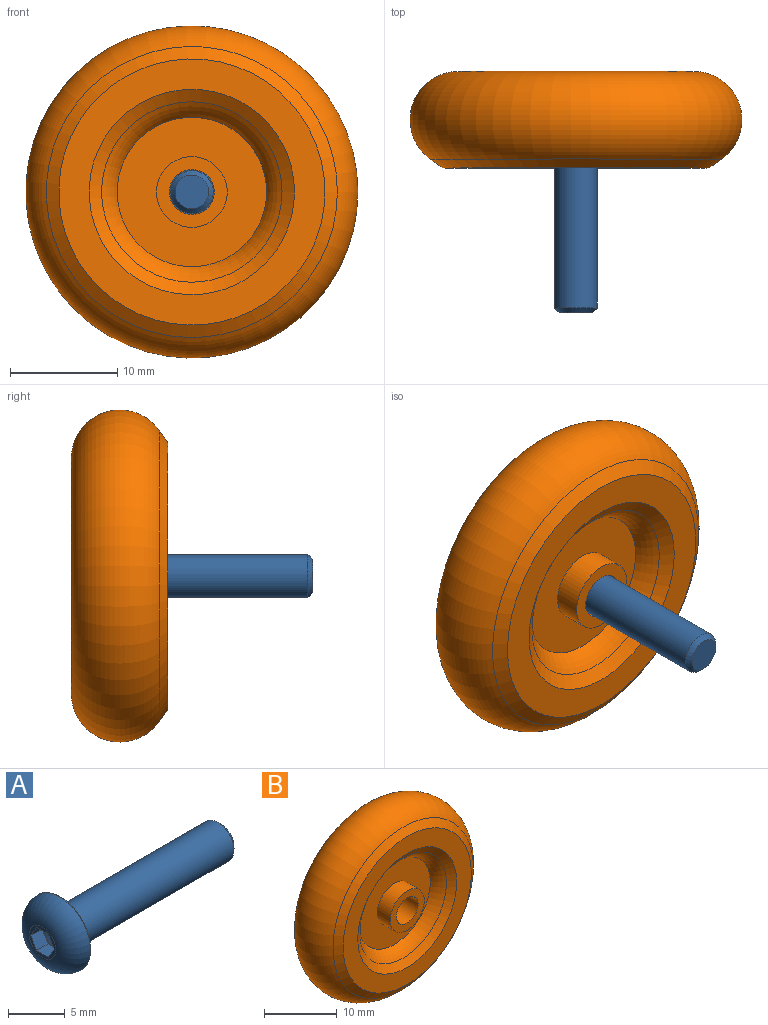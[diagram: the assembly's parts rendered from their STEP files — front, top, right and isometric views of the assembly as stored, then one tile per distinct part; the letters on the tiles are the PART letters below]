
ASSEMBLY  parts=2 mates=1
PART A: 21 faces, bbox 22.2x7.6x7.6 mm
  f0: torus R=1.64mm, axis (-1,0,0), area 64.3mm2, adj f1,f20
  f1: cylinder r=3.8mm len=7.6mm, axis (-1,0,0), area 1mm2, adj f0,f19
  f2: cylinder r=2mm len=19.57mm, axis (-1,0,0), area 245.9mm2, adj f3,f19
  f3: cone r=1.79mm half-angle=45deg, axis (-1,0,0), area 6.8mm2, adj f2,f18
  f4: cylinder r=1.25mm len=2.5mm, axis (-1,0,0), area 0.4mm2, adj f5,f11,f12,f13,f14,f15,f16
  f5: cone r=0.62mm half-angle=60deg, axis (-1,0,0), area 5.7mm2, adj f4
  f6: plane 1.44x1.43mm, normal (0,0,1), area 2.1mm2, adj f7,f8,f13,f14,f20
  f7: plane 1.43x1.25mm, normal (0,-0.87,0.5), area 2.1mm2, adj f6,f9,f12,f13,f20
  f8: plane 1.43x1.25mm, normal (0,0.87,0.5), area 2.1mm2, adj f6,f10,f14,f15,f20
  f9: plane 1.43x1.25mm, normal (0,-0.87,-0.5), area 2.1mm2, adj f7,f11,f12,f17,f20
  f10: plane 1.43x1.25mm, normal (0,0.87,-0.5), area 2.1mm2, adj f8,f15,f16,f17,f20
  f11: plane 1.08x0.63mm, normal (-1,0,0), area 0.1mm2, adj f4,f9,f17
  f12: plane 1.25x0.36mm, normal (-1,0,0), area 0.1mm2, adj f4,f7,f9
  f13: plane 1.08x0.63mm, normal (-1,0,0), area 0.1mm2, adj f4,f6,f7
  f14: plane 1.08x0.63mm, normal (-1,0,0), area 0.1mm2, adj f4,f6,f8
  f15: plane 1.25x0.36mm, normal (-1,0,0), area 0.1mm2, adj f4,f8,f10
  f16: plane 1.08x0.63mm, normal (-1,0,0), area 0.1mm2, adj f4,f10,f17
  f17: plane 1.44x1.43mm, normal (0,0,-1), area 2.1mm2, adj f9,f10,f11,f16,f20
  f18: plane 3.14x3.14mm, normal (1,0,0), area 7.7mm2, adj f3
  f19: plane 7.6x7.6mm, normal (1,0,0), area 32.8mm2, adj f1,f2
  f20: plane 3.28x3.28mm, normal (-1,0,0), area 3mm2, adj f0,f6,f7,f8,f9,f10,f17
PART B: 10 faces, bbox 33.6x9x33.6 mm
  f0: plane 24.84x24.84mm, normal (0,-1,0), area 196.1mm2, adj f1,f9
  f1: cone r=9.58mm half-angle=55deg, axis (0,-1,0), area 80.2mm2, adj f0,f2
  f2: torus R=11mm, axis (0,-1,0), area 107.6mm2, adj f1,f3
  f3: plane 13.94x13.94mm, normal (0,-1,0), area 118.4mm2, adj f2,f4
  f4: cylinder r=3.3mm len=6.6mm, axis (0,-1,0), area 51.8mm2, adj f3,f5
  f5: plane 6.6x6.6mm, normal (0,-1,0), area 20.4mm2, adj f4,f6
  f6: cylinder r=2.1mm len=6.5mm, axis (0,-1,0), area 85.8mm2, adj f5,f7
  f7: plane 13.94x13.94mm, normal (0,1,0), area 138.7mm2, adj f6,f8
  f8: torus R=11mm, axis (0,-1,0), area 1293.2mm2, adj f7,f9
  f9: cone r=12.42mm half-angle=55deg, axis (0,1,0), area 115.9mm2, adj f0,f8
PLACE A rot(axis=(-0.58,0.58,-0.58),120deg) t=(-18.92,-13.4,-6.14)mm fixed
PLACE B rot(axis=(0,-1,0),54.8deg) t=(-58.98,-126.06,-62.83)mm
MATE cylindrical A.f0 <-> B.f1  axis (0,-1,0) through (-18.92,-15.6,-6.14)mm
